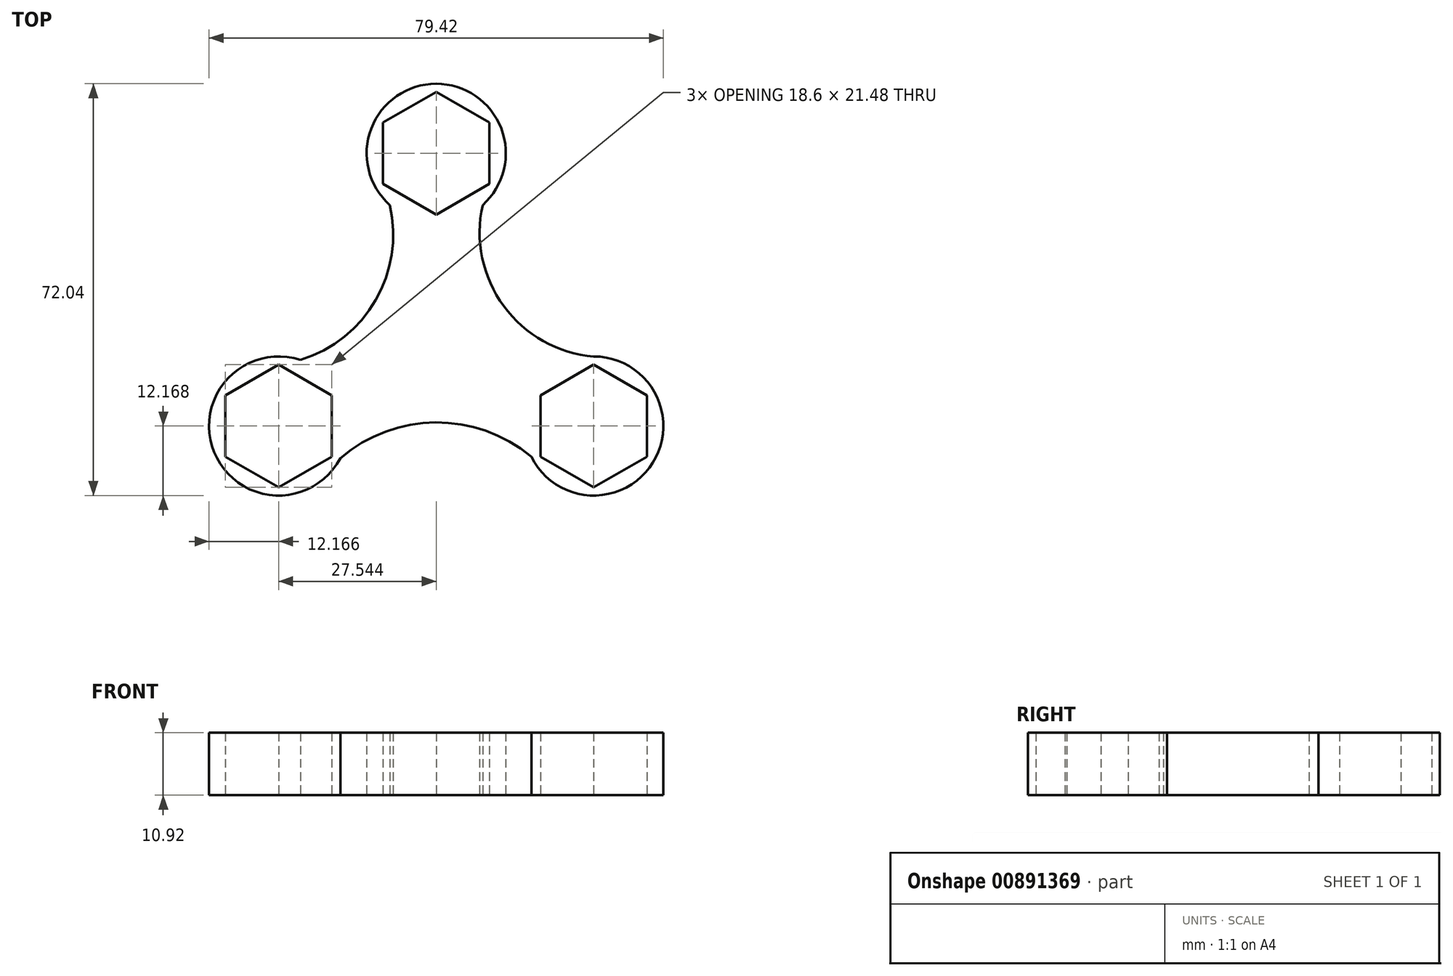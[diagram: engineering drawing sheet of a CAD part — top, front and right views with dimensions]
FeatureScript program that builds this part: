
annotation { "Feature Type Name" : "Feature", "Feature Type Description" : "" }
export const myFeature = defineFeature(function(context is Context, id is Id, definition is map)
    precondition{}
    {
        {
            var Q0;
            Q0=qCreatedBy(makeId("Top.planeOp"),FACE);
            var sketch = newSketch(context, id + "F0", { "sketchPlane" : qUnion([Q0])});
            skCircle(sketch, "E0", {"center": v(0, 0) * mm, "radius": 11.2 * mm});
            skCircle(sketch, "E1.cCircle", {"center": v(0, 34.36) * mm, "radius": 9.3 * mm, "construction": true});
            skLineSegment(sketch, "E1.0", {"start": v(-9.3, 28.99) * mm, "end": v(-9.3, 39.73) * mm});
            skLineSegment(sketch, "E1.1", {"start": v(-9.3, 39.73) * mm, "end": v(0, 45.1) * mm});
            skLineSegment(sketch, "E1.2", {"start": v(0, 45.1) * mm, "end": v(9.3, 39.73) * mm});
            skLineSegment(sketch, "E1.3", {"start": v(9.3, 39.73) * mm, "end": v(9.3, 28.99) * mm});
            skLineSegment(sketch, "E1.4", {"start": v(9.3, 28.99) * mm, "end": v(0, 23.62) * mm});
            skLineSegment(sketch, "E1.5", {"start": v(0, 23.62) * mm, "end": v(-9.3, 28.99) * mm});
            skPoint(sketch, "E1.0.midPoint", {"position": v(-9.3, 34.36) * mm});
            skArc(sketch, "E2", {"start": v(8.11, 25.3) * mm, "mid": v(0, 46.52) * mm, "end": v(-8.1, 25.29) * mm});
            skLineSegment(sketch, "E3.1.0", {"start": v(-18.24, -7.98) * mm, "end": v(-18.24, -18.72) * mm});
            skLineSegment(sketch, "E3.1.1", {"start": v(-18.24, -18.72) * mm, "end": v(-27.54, -24.1) * mm});
            skLineSegment(sketch, "E3.1.2", {"start": v(-27.54, -24.1) * mm, "end": v(-36.84, -18.72) * mm});
            skLineSegment(sketch, "E3.1.3", {"start": v(-36.84, -18.72) * mm, "end": v(-36.84, -7.98) * mm});
            skLineSegment(sketch, "E3.1.4", {"start": v(-36.84, -7.98) * mm, "end": v(-27.54, -2.61) * mm});
            skArc(sketch, "E3.1.5", {"start": v(-23.74, -1.8) * mm, "mid": v(-38.82, -17.92) * mm, "end": v(-16.77, -19) * mm});
            skLineSegment(sketch, "E3.1.6", {"start": v(-27.54, -2.61) * mm, "end": v(-18.24, -7.98) * mm});
            skCircle(sketch, "E3.1.7", {"center": v(-27.54, -13.35) * mm, "radius": 9.3 * mm, "construction": true});
            skLineSegment(sketch, "E3.2.0", {"start": v(18.24, -7.98) * mm, "end": v(27.54, -2.61) * mm});
            skLineSegment(sketch, "E3.2.1", {"start": v(27.54, -2.61) * mm, "end": v(36.84, -7.98) * mm});
            skLineSegment(sketch, "E3.2.2", {"start": v(36.84, -7.98) * mm, "end": v(36.84, -18.72) * mm});
            skLineSegment(sketch, "E3.2.3", {"start": v(36.84, -18.72) * mm, "end": v(27.54, -24.1) * mm});
            skLineSegment(sketch, "E3.2.4", {"start": v(27.54, -24.1) * mm, "end": v(18.24, -18.72) * mm});
            skArc(sketch, "E3.2.5", {"start": v(16.63, -18.72) * mm, "mid": v(37.87, -19.78) * mm, "end": v(27.54, -1.19) * mm});
            skLineSegment(sketch, "E3.2.6", {"start": v(18.24, -18.72) * mm, "end": v(18.24, -7.98) * mm});
            skCircle(sketch, "E3.2.7", {"center": v(27.54, -13.35) * mm, "radius": 9.3 * mm, "construction": true});
            skPoint(sketch, "E3.center", {"position": v(0, 2.55) * mm});
            skArc(sketch, "E4", {"start": v(-23.74, -1.8) * mm, "mid": v(-10.59, 8.66) * mm, "end": v(-8.1, 25.29) * mm});
            skArc(sketch, "E5", {"start": v(8.11, 25.3) * mm, "mid": v(11.8, 7.63) * mm, "end": v(27.54, -1.19) * mm});
            skArc(sketch, "E6", {"start": v(16.63, -18.72) * mm, "mid": v(-0.12, -12.72) * mm, "end": v(-16.77, -19) * mm});
            skSolve(sketch);
        }
        {
            var Q0;
            Q0=makeQuery(id+"F0.imprint","IMPRINT",FACE,{"disambiguationData":[TD([[makeQuery(id+"F0.imprint","IMPRINT",EDGE,{"derivedFrom":sQuery(id+"F0.wireOp",EDGE,"E0")}),-1.0]])]});
            var Q1;
            Q1=makeQuery(id+"F0.imprint","IMPRINT",FACE,{"disambiguationData":[TD([[makeQuery(id+"F0.imprint","IMPRINT",EDGE,{"derivedFrom":sQuery(id+"F0.wireOp",EDGE,"E0")}),1.0]])]});
            extrude(context, id + "F1", {"entities" : qUnion([Q0, Q1]), "depth" : 10.92 * mm, "offsetDistance" : 25.4 * mm});
        }
    });
